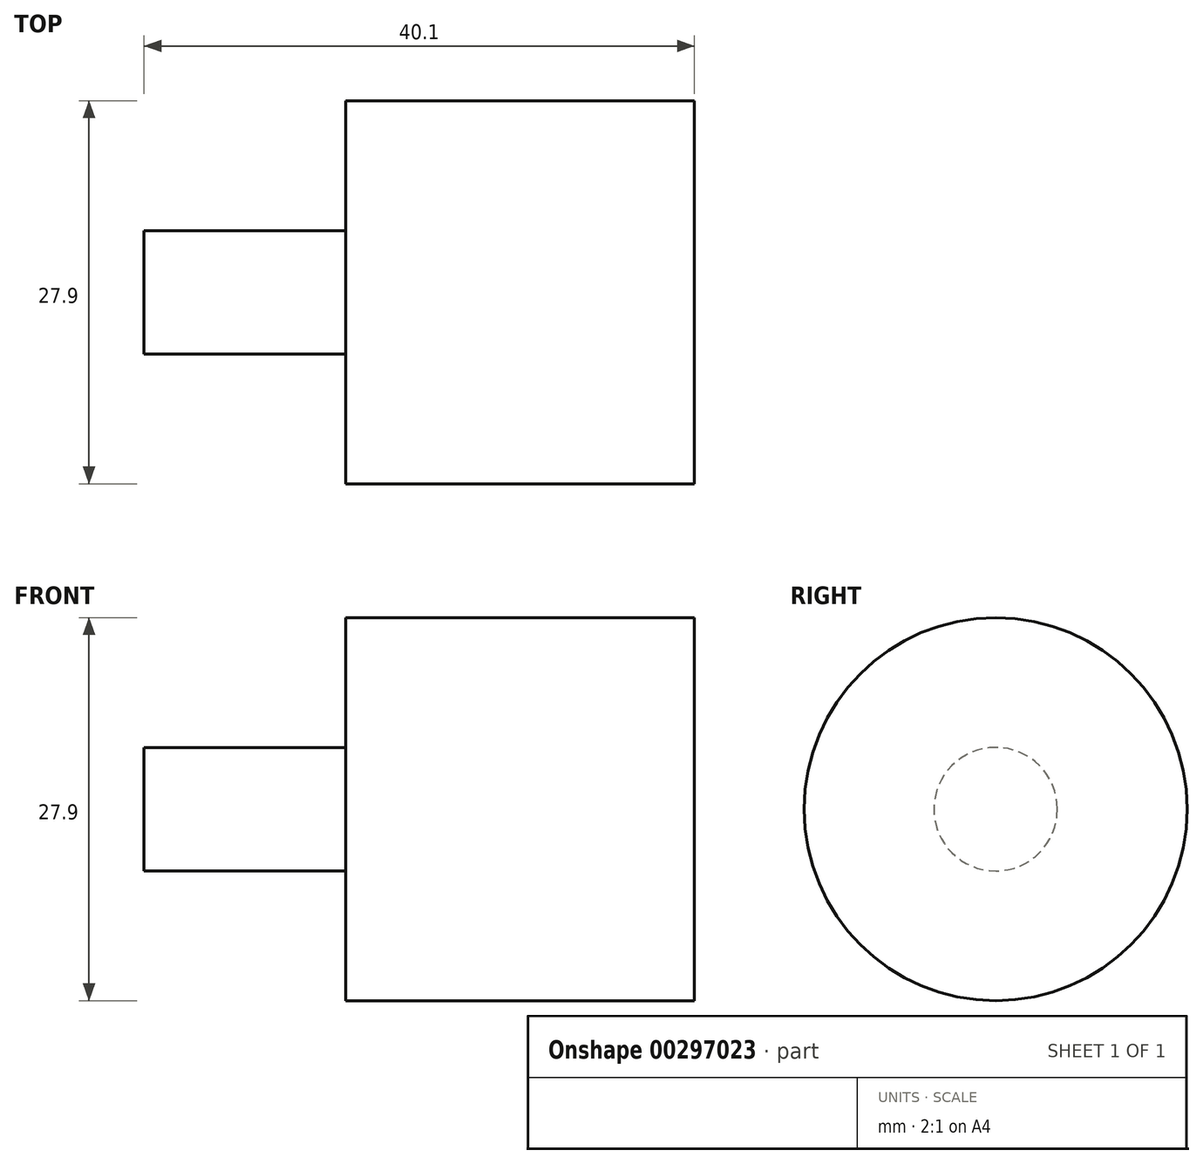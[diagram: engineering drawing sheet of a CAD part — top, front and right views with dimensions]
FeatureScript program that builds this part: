
annotation { "Feature Type Name" : "Feature", "Feature Type Description" : "" }
export const myFeature = defineFeature(function(context is Context, id is Id, definition is map)
    precondition{}
    {
        {
            var Q0;
            Q0=qCreatedBy(makeId("Front.planeOp"),FACE);
            var sketch = newSketch(context, id + "F0", { "sketchPlane" : qUnion([Q0])});
            skLineSegment(sketch, "E0.bottom", {"start": v(-25.4, 13.95) * mm, "end": v(0, 13.95) * mm});
            skLineSegment(sketch, "E0.top", {"start": v(-25.4, -13.95) * mm, "end": v(0, -13.95) * mm});
            skLineSegment(sketch, "E0.left", {"start": v(-25.4, 13.95) * mm, "end": v(-25.4, -13.95) * mm});
            skLineSegment(sketch, "E0.right", {"start": v(0, 13.95) * mm, "end": v(0, -13.95) * mm});
            skLineSegment(sketch, "E1.bottom", {"start": v(-40.1, -4.5) * mm, "end": v(-25.4, -4.5) * mm});
            skLineSegment(sketch, "E1.top", {"start": v(-40.1, 4.5) * mm, "end": v(-25.4, 4.5) * mm});
            skLineSegment(sketch, "E1.left", {"start": v(-40.1, 4.5) * mm, "end": v(-40.1, -4.5) * mm});
            skLineSegment(sketch, "E1.right", {"start": v(-25.4, 4.5) * mm, "end": v(-25.4, -4.5) * mm});
            skLineSegment(sketch, "E2", {"start": v(0, 0) * mm, "end": v(-40.1, 0) * mm});
            skSolve(sketch);
        }
        {
            var Q0;
            {var subQ1=sQuery(id+"F0.wireOp",EDGE,"E0.bottom");Q0=makeQuery(id+"F0.imprint","IMPRINT",FACE,{"disambiguationData":[TD([[makeQuery(id+"F0.imprint","IMPRINT",EDGE,{"derivedFrom":subQ1}),-1.0]])]});}
            var Q1;
            {var subQ0=sQuery(id+"F0.wireOp",EDGE,"E1.top");Q1=makeQuery(id+"F0.imprint","IMPRINT",FACE,{"disambiguationData":[TD([[makeQuery(id+"F0.imprint","IMPRINT",EDGE,{"derivedFrom":subQ0}),-1.0]])]});}
            var Q2;
            Q2=sQuery(id+"F0.wireOp",EDGE,"E2");
            revolve(context, id + "F1", {"entities" : qUnion([Q0, Q1]), "axis" : qUnion([Q2]), "revolveType" : RevolveType.FULL});
        }
    });
